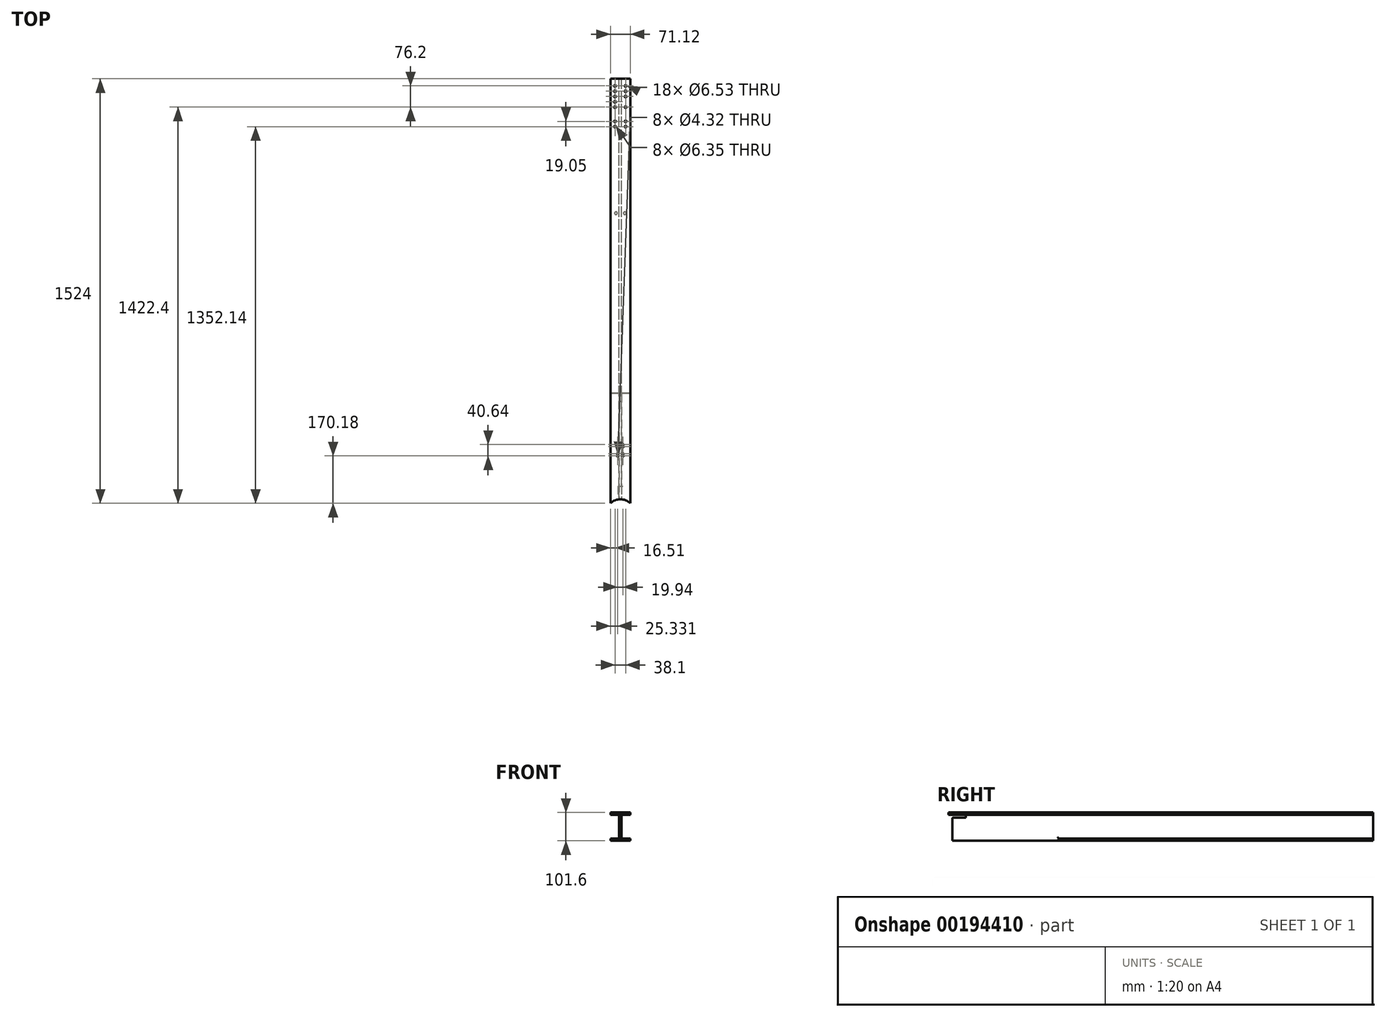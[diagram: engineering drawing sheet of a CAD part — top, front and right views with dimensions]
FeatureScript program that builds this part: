
annotation { "Feature Type Name" : "Feature", "Feature Type Description" : "" }
export const myFeature = defineFeature(function(context is Context, id is Id, definition is map)
    precondition{}
    {
        {
            var Q0;
            Q0=qCreatedBy(makeId("Front.planeOp"),FACE);
            var sketch = newSketch(context, id + "F0", { "sketchPlane" : qUnion([Q0])});
            skLineSegment(sketch, "E0.bottom", {"start": v(35.56, -50.8) * mm, "end": v(-35.56, -50.8) * mm});
            skLineSegment(sketch, "E0.top", {"start": v(35.56, 50.8) * mm, "end": v(-35.56, 50.8) * mm});
            skLineSegment(sketch, "E0.left", {"start": v(35.56, -50.8) * mm, "end": v(35.56, -42.42) * mm});
            skLineSegment(sketch, "E0.right", {"start": v(-35.56, -50.8) * mm, "end": v(-35.56, -42.42) * mm});
            skPoint(sketch, "E0.middle", {"position": v(0, 0) * mm});
            skLineSegment(sketch, "E1", {"start": v(-35.56, 50.8) * mm, "end": v(-35.56, 42.42) * mm});
            skLineSegment(sketch, "E2", {"start": v(-35.56, 42.42) * mm, "end": v(-4.2, 42.42) * mm});
            skLineSegment(sketch, "E3", {"start": v(0, 50.8) * mm, "end": v(-4.2, 50.8) * mm});
            skLineSegment(sketch, "E4", {"start": v(-4.2, 42.42) * mm, "end": v(-4.2, 0) * mm});
            skLineSegment(sketch, "E5.MirrorCS", {"start": v(4.2, 42.42) * mm, "end": v(4.2, 0) * mm});
            skLineSegment(sketch, "E6.MirrorCS", {"start": v(35.56, 50.8) * mm, "end": v(35.56, 42.42) * mm});
            skLineSegment(sketch, "E7.MirrorCS", {"start": v(-35.56, -42.42) * mm, "end": v(-4.2, -42.42) * mm});
            skLineSegment(sketch, "E8.MirrorCS", {"start": v(-4.2, -42.42) * mm, "end": v(-4.2, 0) * mm});
            skLineSegment(sketch, "E9.MirrorCS", {"start": v(4.2, -42.42) * mm, "end": v(4.2, 0) * mm});
            skPoint(sketch, "E10.orphan", {"position": v(0, -50.8) * mm});
            skLineSegment(sketch, "E11.trimOffspring", {"start": v(4.2, -42.42) * mm, "end": v(35.56, -42.42) * mm});
            skLineSegment(sketch, "E12.trimOffspring", {"start": v(4.2, 42.42) * mm, "end": v(35.56, 42.42) * mm});
            skLineSegment(sketch, "E13.trimOffspring", {"start": v(35.56, 42.42) * mm, "end": v(35.56, 50.8) * mm});
            skLineSegment(sketch, "E14.trimOffspring", {"start": v(-35.56, 42.42) * mm, "end": v(-35.56, 50.8) * mm});
            skSolve(sketch);
        }
        {
            var Q0;
            Q0=makeQuery(id+"F0.imprint","IMPRINT",FACE,{"disambiguationData":[TD([[makeQuery(id+"F0.imprint","IMPRINT",EDGE,{"derivedFrom":sQuery(id+"F0.wireOp",EDGE,"E0.bottom")}),-1.0]])]});
            extrude(context, id + "F1", {"entities" : qUnion([Q0]), "depth" : 1524 * mm});
        }
        {
            var Q0;
            Q0=makeQuery(id+"F1.opExtrude","SWEPT_EDGE",EDGE,{"disambiguationData":[OSD([sQuery(id+"F0.wireOp",EDGE,"E5.MirrorCS"),sQuery(id+"F0.wireOp",EDGE,"E12.trimOffspring")])]});
            var Q1;
            Q1=makeQuery(id+"F1.opExtrude","SWEPT_EDGE",EDGE,{"disambiguationData":[OSD([sQuery(id+"F0.wireOp",EDGE,"E9.MirrorCS"),sQuery(id+"F0.wireOp",EDGE,"E11.trimOffspring")])]});
            var Q2;
            Q2=makeQuery(id+"F1.opExtrude","SWEPT_EDGE",EDGE,{"disambiguationData":[OSD([sQuery(id+"F0.wireOp",EDGE,"E7.MirrorCS"),sQuery(id+"F0.wireOp",EDGE,"E8.MirrorCS")])]});
            var Q3;
            Q3=makeQuery(id+"F1.opExtrude","SWEPT_EDGE",EDGE,{"disambiguationData":[OSD([sQuery(id+"F0.wireOp",EDGE,"E2"),sQuery(id+"F0.wireOp",EDGE,"E4")])]});
            fillet(context, id + "F2", {"entities" : qUnion([Q0, Q1, Q2, Q3]), "radius" : 5.08 * mm, "tangentPropagation" : true, "allowEdgeOverflow" : false});
        }
        {
            var Q0;
            Q0=makeQuery(id+"F1.opExtrude","SWEPT_FACE",FACE,{"disambiguationData":[OSD([sQuery(id+"F0.wireOp",EDGE,"E0.top"),sQuery(id+"F0.wireOp",EDGE,"E3")])]});
            var sketch = newSketch(context, id + "F3", { "sketchPlane" : qUnion([Q0])});
            skLineSegment(sketch, "E15", {"start": v(0, -1524) * mm, "end": v(0, -1560.28) * mm});
            skPoint(sketch, "E15.endSnap0", {"position": v(0, -1524) * mm});
            skLineSegment(sketch, "E16", {"start": v(35.56, -1524) * mm, "end": v(0, -1560.28) * mm});
            skCircle(sketch, "E17", {"center": v(0, -1560.28) * mm, "radius": 50.8 * mm});
            skLineSegment(sketch, "E18.trimOffspring", {"start": v(0, -1611.08) * mm, "end": v(0, -1676.71) * mm});
            skSolve(sketch);
        }
        {
            var Q0;
            {var subQ6=sQuery(id+"F3.wireOp",EDGE,"E15");Q0=makeQuery(id+"F3.imprint","IMPRINT",FACE,{"disambiguationData":[TD([[makeQuery(id+"F3.imprint","IMPRINT",EDGE,{"derivedFrom":subQ6}),-1.0]])]});}
            var Q1;
            {var subQ0=sQuery(id+"F3.wireOp",EDGE,"E15");Q1=makeQuery(id+"F3.imprint","IMPRINT",FACE,{"disambiguationData":[TD([[makeQuery(id+"F3.imprint","IMPRINT",EDGE,{"derivedFrom":subQ0}),1.0]])]});}
            var Q2;
            {var subQ1=sQuery(id+"F0.wireOp",EDGE,"E0.top");var subQ2=makeQuery(id+"F1.opExtrude","CAP_EDGE",EDGE,{"disambiguationData":[OSD([subQ1,sQuery(id+"F0.wireOp",EDGE,"E3")])],"isStart":false});var subQ5=makeQuery(id+"F3.imprint","INTERSECT",VERTEX,{"derivedFrom":[subQ2,sQuery(id+"F3.wireOp",EDGE,"E15")]});Q2=makeQuery(id+"F3.imprint","IMPRINT",FACE,{"disambiguationData":[TD([[makeQuery(id+"F3.imprint","IMPRINT",EDGE,{"disambiguationData":[TD([[subQ5,-1.0]])],"derivedFrom":subQ2}),-1.0]])]});}
            extrude(context, id + "F4", {"entities" : qUnion([Q0, Q1, Q2]), "operationType" : NewBodyOperationType.REMOVE, "oppositeDirection" : true, "depth" : 101.6 * mm});
        }
        {
            var Q0;
            Q0=makeQuery(id+"F1.opExtrude","SWEPT_FACE",FACE,{"disambiguationData":[OSD([sQuery(id+"F0.wireOp",EDGE,"E5.MirrorCS"),sQuery(id+"F0.wireOp",EDGE,"E9.MirrorCS")])]});
            var sketch = newSketch(context, id + "F5", { "sketchPlane" : qUnion([Q0])});
            skSolve(sketch);
        }
        {
            var Q0;
            {var subQ0=sQuery(id+"F0.wireOp",EDGE,"E9.MirrorCS");var subQ1=sQuery(id+"F0.wireOp",EDGE,"E5.MirrorCS");Q0=makeQuery(id+"F5.imprint","IMPRINT",FACE,{"disambiguationData":[TD([[makeQuery(id+"F5.imprint","IMPRINT",EDGE,{"derivedFrom":makeQuery(id+"F1.opExtrude","CAP_EDGE",EDGE,{"disambiguationData":[OSD([subQ1,subQ0])],"isStart":true})}),1.0]])]});}
            var sketch = newSketch(context, id + "F6", { "sketchPlane" : qUnion([Q0])});
            skLineSegment(sketch, "E19", {"start": v(-1510.33, 42.42) * mm, "end": v(-1510.33, 32.26) * mm});
            skLineSegment(sketch, "E20", {"start": v(-1510.33, 32.26) * mm, "end": v(-1462.07, 32.26) * mm});
            skLineSegment(sketch, "E21", {"start": v(-1462.07, 32.26) * mm, "end": v(-1462.07, 42.42) * mm});
            skLineSegment(sketch, "E22", {"start": v(-1462.07, 42.42) * mm, "end": v(-1510.33, 42.42) * mm});
            skSolve(sketch);
        }
        {
            var Q0;
            Q0=qSketchRegion(id+"F6",true);
            extrude(context, id + "F7", {"entities" : qUnion([Q0]), "operationType" : NewBodyOperationType.REMOVE, "endBound" : BoundingType.SYMMETRIC, "oppositeDirection" : true, "depth" : 25.4 * mm});
        }
        {
            var Q0;
            Q0=makeQuery(id+"F7.boolean.opBoolean","INTERSECT",EDGE,{"derivedFrom":[makeQuery(id+"F4.boolean.opBoolean","COPY",FACE,{"derivedFrom":makeQuery(id+"F4.opExtrude","SWEPT_FACE",FACE,{"disambiguationData":[OSD([sQuery(id+"F3.wireOp",EDGE,"E17")])]})}),makeQuery(id+"F7.opExtrude","SWEPT_FACE",FACE,{"disambiguationData":[OSD([sQuery(id+"F6.wireOp",EDGE,"E20")])]})]});
            chamfer(context, id + "F8", {"entities" : qUnion([Q0]), "width" : 1.27 * mm, "tangentPropagation" : true});
        }
        {
            var Q0;
            Q0=makeQuery(id+"F1.opExtrude","SWEPT_FACE",FACE,{"disambiguationData":[OSD([sQuery(id+"F0.wireOp",EDGE,"E0.top"),sQuery(id+"F0.wireOp",EDGE,"E3")])]});
            var sketch = newSketch(context, id + "F9", { "sketchPlane" : qUnion([Q0])});
            skLineSegment(sketch, "E23", {"start": v(-0.26, -1524) * mm, "end": v(-0.26, -0.03) * mm});
            skLineSegment(sketch, "E24.bottom", {"start": v(9.71, -1353.82) * mm, "end": v(-10.23, -1353.82) * mm});
            skLineSegment(sketch, "E24.top", {"start": v(9.71, -1313.18) * mm, "end": v(-10.23, -1313.18) * mm});
            skLineSegment(sketch, "E25.bottom", {"start": v(9.71, -1346.2) * mm, "end": v(-10.23, -1346.2) * mm});
            skLineSegment(sketch, "E25.top", {"start": v(9.71, -1320.8) * mm, "end": v(-10.23, -1320.8) * mm});
            skLineSegment(sketch, "E26", {"start": v(35.56, -1524) * mm, "end": v(-35.56, -1524) * mm});
            skLineSegment(sketch, "E27", {"start": v(-0.26, -1524) * mm, "end": v(-0.26, -1353.82) * mm});
            skLineSegment(sketch, "E28", {"start": v(-0.26, -1353.82) * mm, "end": v(-0.26, -1346.2) * mm});
            skLineSegment(sketch, "E29", {"start": v(-0.26, -1346.2) * mm, "end": v(-0.26, -1320.8) * mm});
            skLineSegment(sketch, "E30", {"start": v(-0.26, -1320.8) * mm, "end": v(-0.26, -1313.18) * mm});
            skSolve(sketch);
        }
        {
            var Q0;
            Q0=sQuery(id+"F9.wireOp",VERTEX,"E24.bottom.end");
            var Q1;
            Q1=sQuery(id+"F9.wireOp",VERTEX,"E25.bottom.end");
            var Q2;
            Q2=sQuery(id+"F9.wireOp",VERTEX,"E25.top.end");
            var Q3;
            Q3=sQuery(id+"F9.wireOp",VERTEX,"E24.top.end");
            var Q4;
            Q4=sQuery(id+"F9.wireOp",VERTEX,"E24.top.start");
            var Q5;
            Q5=sQuery(id+"F9.wireOp",VERTEX,"E25.top.start");
            var Q6;
            Q6=sQuery(id+"F9.wireOp",VERTEX,"E25.bottom.start");
            var Q7;
            Q7=sQuery(id+"F9.wireOp",VERTEX,"E24.bottom.start");
            var Q8;
            Q8=makeQuery(id+"F1.opExtrude","SWEPT_BODY",BODY,{"disambiguationData":[OSD([sQuery(id+"F0.wireOp",EDGE,"E0.bottom"),sQuery(id+"F0.wireOp",EDGE,"E0.top"),sQuery(id+"F0.wireOp",EDGE,"E0.left"),sQuery(id+"F0.wireOp",EDGE,"E0.right"),sQuery(id+"F0.wireOp",EDGE,"E2"),sQuery(id+"F0.wireOp",EDGE,"E3"),sQuery(id+"F0.wireOp",EDGE,"E4"),sQuery(id+"F0.wireOp",EDGE,"E5.MirrorCS"),sQuery(id+"F0.wireOp",EDGE,"E7.MirrorCS"),sQuery(id+"F0.wireOp",EDGE,"E8.MirrorCS"),sQuery(id+"F0.wireOp",EDGE,"E9.MirrorCS"),sQuery(id+"F0.wireOp",EDGE,"E11.trimOffspring"),sQuery(id+"F0.wireOp",EDGE,"E12.trimOffspring"),sQuery(id+"F0.wireOp",EDGE,"E13.trimOffspring"),sQuery(id+"F0.wireOp",EDGE,"E14.trimOffspring")])]});
            hole(context, id + "F10", {"style" : HoleStyle.SIMPLE, "endStyle" : HoleEndStyle.BLIND, "standardTappedOrClearance" : lookupTablePath({ "standard" : "ANSI", "fit" : "Close", "size" : "#8", "type" : "Clearance" }), "standardBlindInLast" : lookupTablePath({ "fit" : "Close", "standard" : "ANSI", "size" : "#8", "type" : "Clearance" }), "holeDiameter" : 4.32 * mm, "holeDepth" : 25.4 * mm, "locations" : qUnion([Q0, Q1, Q2, Q3, Q4, Q5, Q6, Q7]), "scope" : qUnion([Q8])});
        }
        {
            var Q0;
            Q0=makeQuery(id+"F1.opExtrude","SWEPT_FACE",FACE,{"disambiguationData":[OSD([sQuery(id+"F0.wireOp",EDGE,"E0.bottom")])]});
            var sketch = newSketch(context, id + "F11", { "sketchPlane" : qUnion([Q0])});
            skLineSegment(sketch, "E31", {"start": v(4.2, 1509.65) * mm, "end": v(4.2, 1128.65) * mm});
            skLineSegment(sketch, "E32.bottom", {"start": v(4.2, 1128.65) * mm, "end": v(39.68, 1128.65) * mm});
            skLineSegment(sketch, "E32.top", {"start": v(4.2, 1528.41) * mm, "end": v(39.68, 1528.41) * mm});
            skLineSegment(sketch, "E32.left", {"start": v(4.2, 1128.65) * mm, "end": v(4.2, 1528.41) * mm});
            skLineSegment(sketch, "E32.right", {"start": v(39.68, 1128.65) * mm, "end": v(39.68, 1528.41) * mm});
            skLineSegment(sketch, "E33", {"start": v(0, 1526.52) * mm, "end": v(0, 1517.43) * mm});
            skLineSegment(sketch, "E34.MirrorCS", {"start": v(-4.2, 1528.41) * mm, "end": v(-39.68, 1528.41) * mm});
            skLineSegment(sketch, "E35.MirrorCS", {"start": v(-39.68, 1128.65) * mm, "end": v(-39.68, 1528.41) * mm});
            skLineSegment(sketch, "E36.MirrorCS", {"start": v(-4.2, 1128.65) * mm, "end": v(-4.2, 1528.41) * mm});
            skLineSegment(sketch, "E37.MirrorCS", {"start": v(-4.2, 1128.65) * mm, "end": v(-39.68, 1128.65) * mm});
            skSolve(sketch);
        }
        {
            var Q0;
            Q0=qSketchRegion(id+"F11",true);
            extrude(context, id + "F12", {"entities" : qUnion([Q0]), "operationType" : NewBodyOperationType.REMOVE, "oppositeDirection" : true, "depth" : 25.4 * mm});
        }
        {
            var Q0;
            Q0=makeQuery(id+"F12.boolean.opBoolean","COPY",EDGE,{"derivedFrom":makeQuery(id+"F12.opExtrude","SWEPT_EDGE",EDGE,{"disambiguationData":[OSD([sQuery(id+"F11.wireOp",EDGE,"E32.bottom"),sQuery(id+"F11.wireOp",EDGE,"E32.left")])]})});
            var Q1;
            Q1=makeQuery(id+"F12.boolean.opBoolean","COPY",EDGE,{"derivedFrom":makeQuery(id+"F12.opExtrude","SWEPT_EDGE",EDGE,{"disambiguationData":[OSD([sQuery(id+"F11.wireOp",EDGE,"E36.MirrorCS"),sQuery(id+"F11.wireOp",EDGE,"E37.MirrorCS")])]})});
            fillet(context, id + "F13", {"entities" : qUnion([Q0, Q1]), "radius" : 3.17 * mm, "tangentPropagation" : true, "allowEdgeOverflow" : false});
        }
        {
            var Q0;
            Q0=makeQuery(id+"F1.opExtrude","SWEPT_FACE",FACE,{"disambiguationData":[OSD([sQuery(id+"F0.wireOp",EDGE,"E0.bottom")])]});
            var sketch = newSketch(context, id + "F14", { "sketchPlane" : qUnion([Q0])});
            skLineSegment(sketch, "E38", {"start": v(0, 0) * mm, "end": v(0, 482.6) * mm});
            skPoint(sketch, "E38.endSnap0", {"position": v(0, 0) * mm});
            skLineSegment(sketch, "E39", {"start": v(0, 482.6) * mm, "end": v(15.88, 482.6) * mm});
            skLineSegment(sketch, "E40", {"start": v(15.88, 482.6) * mm, "end": v(-15.88, 482.6) * mm});
            skSolve(sketch);
        }
        {
            var Q0;
            Q0=sQuery(id+"F14.wireOp",VERTEX,"E40.start");
            var Q1;
            Q1=sQuery(id+"F14.wireOp",VERTEX,"E40.end");
            var Q2;
            Q2=makeQuery(id+"F1.opExtrude","SWEPT_BODY",BODY,{"disambiguationData":[OSD([sQuery(id+"F0.wireOp",EDGE,"E0.bottom"),sQuery(id+"F0.wireOp",EDGE,"E0.top"),sQuery(id+"F0.wireOp",EDGE,"E0.left"),sQuery(id+"F0.wireOp",EDGE,"E0.right"),sQuery(id+"F0.wireOp",EDGE,"E2"),sQuery(id+"F0.wireOp",EDGE,"E3"),sQuery(id+"F0.wireOp",EDGE,"E4"),sQuery(id+"F0.wireOp",EDGE,"E5.MirrorCS"),sQuery(id+"F0.wireOp",EDGE,"E7.MirrorCS"),sQuery(id+"F0.wireOp",EDGE,"E8.MirrorCS"),sQuery(id+"F0.wireOp",EDGE,"E9.MirrorCS"),sQuery(id+"F0.wireOp",EDGE,"E11.trimOffspring"),sQuery(id+"F0.wireOp",EDGE,"E12.trimOffspring"),sQuery(id+"F0.wireOp",EDGE,"E13.trimOffspring"),sQuery(id+"F0.wireOp",EDGE,"E14.trimOffspring")])]});
            hole(context, id + "F15", {"style" : HoleStyle.SIMPLE, "endStyle" : HoleEndStyle.BLIND, "standardTappedOrClearance" : lookupTablePath({ "standard" : "ANSI", "fit" : "Close", "size" : "3/8", "type" : "Clearance" }), "standardBlindInLast" : lookupTablePath({ "fit" : "Close", "standard" : "ANSI", "size" : "3/8", "type" : "Clearance" }), "holeDiameter" : 9.8 * mm, "holeDepth" : 25.4 * mm, "locations" : qUnion([Q0, Q1]), "scope" : qUnion([Q2])});
        }
        {
            var Q0;
            Q0=makeQuery(id+"F1.opExtrude","SWEPT_FACE",FACE,{"disambiguationData":[OSD([sQuery(id+"F0.wireOp",EDGE,"E0.top"),sQuery(id+"F0.wireOp",EDGE,"E3")])]});
            var sketch = newSketch(context, id + "F16", { "sketchPlane" : qUnion([Q0])});
            skLineSegment(sketch, "E41", {"start": v(0, 0) * mm, "end": v(0, -25.4) * mm});
            skLineSegment(sketch, "E42", {"start": v(0, -25.4) * mm, "end": v(19.05, -25.4) * mm});
            skLineSegment(sketch, "E43", {"start": v(19.05, -25.4) * mm, "end": v(19.05, -44.45) * mm});
            skLineSegment(sketch, "E44", {"start": v(19.05, -44.45) * mm, "end": v(19.05, -63.5) * mm});
            skLineSegment(sketch, "E45", {"start": v(19.05, -63.5) * mm, "end": v(19.05, -82.55) * mm});
            skLineSegment(sketch, "E46", {"start": v(19.05, -82.55) * mm, "end": v(19.05, -101.6) * mm});
            skLineSegment(sketch, "E47.MirrorCS", {"start": v(-19.05, -25.4) * mm, "end": v(-19.05, -44.45) * mm});
            skLineSegment(sketch, "E48.MirrorCS", {"start": v(-19.05, -44.45) * mm, "end": v(-19.05, -63.5) * mm});
            skLineSegment(sketch, "E49.MirrorCS", {"start": v(-19.05, -63.5) * mm, "end": v(-19.05, -82.55) * mm});
            skLineSegment(sketch, "E50.MirrorCS", {"start": v(-19.05, -82.55) * mm, "end": v(-19.05, -101.6) * mm});
            skLineSegment(sketch, "E51.MirrorCS", {"start": v(0, -25.4) * mm, "end": v(-19.05, -25.4) * mm});
            skSolve(sketch);
        }
        {
            var Q0;
            Q0=sQuery(id+"F16.wireOp",VERTEX,"E50.MirrorCS.start");
            var Q1;
            Q1=sQuery(id+"F16.wireOp",VERTEX,"E50.MirrorCS.end");
            var Q2;
            Q2=sQuery(id+"F16.wireOp",VERTEX,"E49.MirrorCS.start");
            var Q3;
            Q3=sQuery(id+"F16.wireOp",VERTEX,"E48.MirrorCS.start");
            var Q4;
            Q4=sQuery(id+"F16.wireOp",VERTEX,"E51.MirrorCS.end");
            var Q5;
            Q5=sQuery(id+"F16.wireOp",VERTEX,"E43.start");
            var Q6;
            Q6=sQuery(id+"F16.wireOp",VERTEX,"E44.start");
            var Q7;
            Q7=sQuery(id+"F16.wireOp",VERTEX,"E45.start");
            var Q8;
            Q8=sQuery(id+"F16.wireOp",VERTEX,"E46.end");
            var Q9;
            Q9=sQuery(id+"F16.wireOp",VERTEX,"E46.end");
            var Q10;
            Q10=makeQuery(id+"F1.opExtrude","SWEPT_BODY",BODY,{"disambiguationData":[OSD([sQuery(id+"F0.wireOp",EDGE,"E0.bottom"),sQuery(id+"F0.wireOp",EDGE,"E0.top"),sQuery(id+"F0.wireOp",EDGE,"E0.left"),sQuery(id+"F0.wireOp",EDGE,"E0.right"),sQuery(id+"F0.wireOp",EDGE,"E2"),sQuery(id+"F0.wireOp",EDGE,"E3"),sQuery(id+"F0.wireOp",EDGE,"E4"),sQuery(id+"F0.wireOp",EDGE,"E5.MirrorCS"),sQuery(id+"F0.wireOp",EDGE,"E7.MirrorCS"),sQuery(id+"F0.wireOp",EDGE,"E8.MirrorCS"),sQuery(id+"F0.wireOp",EDGE,"E9.MirrorCS"),sQuery(id+"F0.wireOp",EDGE,"E11.trimOffspring"),sQuery(id+"F0.wireOp",EDGE,"E12.trimOffspring"),sQuery(id+"F0.wireOp",EDGE,"E13.trimOffspring"),sQuery(id+"F0.wireOp",EDGE,"E14.trimOffspring")])]});
            hole(context, id + "F17", {"style" : HoleStyle.SIMPLE, "endStyle" : HoleEndStyle.THROUGH, "standardTappedOrClearance" : lookupTablePath({ "standard" : "ANSI", "fit" : "Close", "size" : "1/4", "type" : "Clearance" }), "standardBlindInLast" : lookupTablePath({ "fit" : "Close", "standard" : "ANSI", "size" : "1/4", "type" : "Clearance" }), "holeDiameter" : 6.53 * mm, "locations" : qUnion([Q0, Q1, Q2, Q3, Q4, Q5, Q6, Q7, Q8, Q9]), "scope" : qUnion([Q10]), "isTappedThrough" : true});
        }
        {
            var Q0;
            Q0=makeQuery(id+"F1.opExtrude","SWEPT_FACE",FACE,{"disambiguationData":[OSD([sQuery(id+"F0.wireOp",EDGE,"E0.top"),sQuery(id+"F0.wireOp",EDGE,"E3")])]});
            var sketch = newSketch(context, id + "F18", { "sketchPlane" : qUnion([Q0])});
            skLineSegment(sketch, "E52", {"start": v(-19.05, -101.6) * mm, "end": v(-19.05, -152.8) * mm});
            skLineSegment(sketch, "E53", {"start": v(-19.05, -152.8) * mm, "end": v(-19.05, -171.86) * mm});
            skLineSegment(sketch, "E54", {"start": v(-19.05, -171.86) * mm, "end": v(-19.05, -190.9) * mm});
            skLineSegment(sketch, "E55", {"start": v(-19.05, -190.9) * mm, "end": v(19.05, -190.9) * mm});
            skLineSegment(sketch, "E56", {"start": v(19.05, -190.9) * mm, "end": v(19.05, -171.86) * mm});
            skLineSegment(sketch, "E57", {"start": v(19.05, -171.86) * mm, "end": v(19.05, -152.8) * mm});
            skSolve(sketch);
        }
        {
            var Q0;
            Q0=sQuery(id+"F18.wireOp",VERTEX,"E53.start");
            var Q1;
            Q1=sQuery(id+"F18.wireOp",VERTEX,"E54.start");
            var Q2;
            Q2=sQuery(id+"F18.wireOp",VERTEX,"E57.end");
            var Q3;
            Q3=sQuery(id+"F18.wireOp",VERTEX,"E57.start");
            var Q4;
            Q4=makeQuery(id+"F1.opExtrude","SWEPT_BODY",BODY,{"disambiguationData":[OSD([sQuery(id+"F0.wireOp",EDGE,"E0.bottom"),sQuery(id+"F0.wireOp",EDGE,"E0.top"),sQuery(id+"F0.wireOp",EDGE,"E0.left"),sQuery(id+"F0.wireOp",EDGE,"E0.right"),sQuery(id+"F0.wireOp",EDGE,"E2"),sQuery(id+"F0.wireOp",EDGE,"E3"),sQuery(id+"F0.wireOp",EDGE,"E4"),sQuery(id+"F0.wireOp",EDGE,"E5.MirrorCS"),sQuery(id+"F0.wireOp",EDGE,"E7.MirrorCS"),sQuery(id+"F0.wireOp",EDGE,"E8.MirrorCS"),sQuery(id+"F0.wireOp",EDGE,"E9.MirrorCS"),sQuery(id+"F0.wireOp",EDGE,"E11.trimOffspring"),sQuery(id+"F0.wireOp",EDGE,"E12.trimOffspring"),sQuery(id+"F0.wireOp",EDGE,"E13.trimOffspring"),sQuery(id+"F0.wireOp",EDGE,"E14.trimOffspring")])]});
            hole(context, id + "F19", {"style" : HoleStyle.SIMPLE, "endStyle" : HoleEndStyle.THROUGH, "holeDiameter" : 6.35 * mm, "locations" : qUnion([Q0, Q1, Q2, Q3]), "scope" : qUnion([Q4]), "isTappedThrough" : true});
        }
    });
